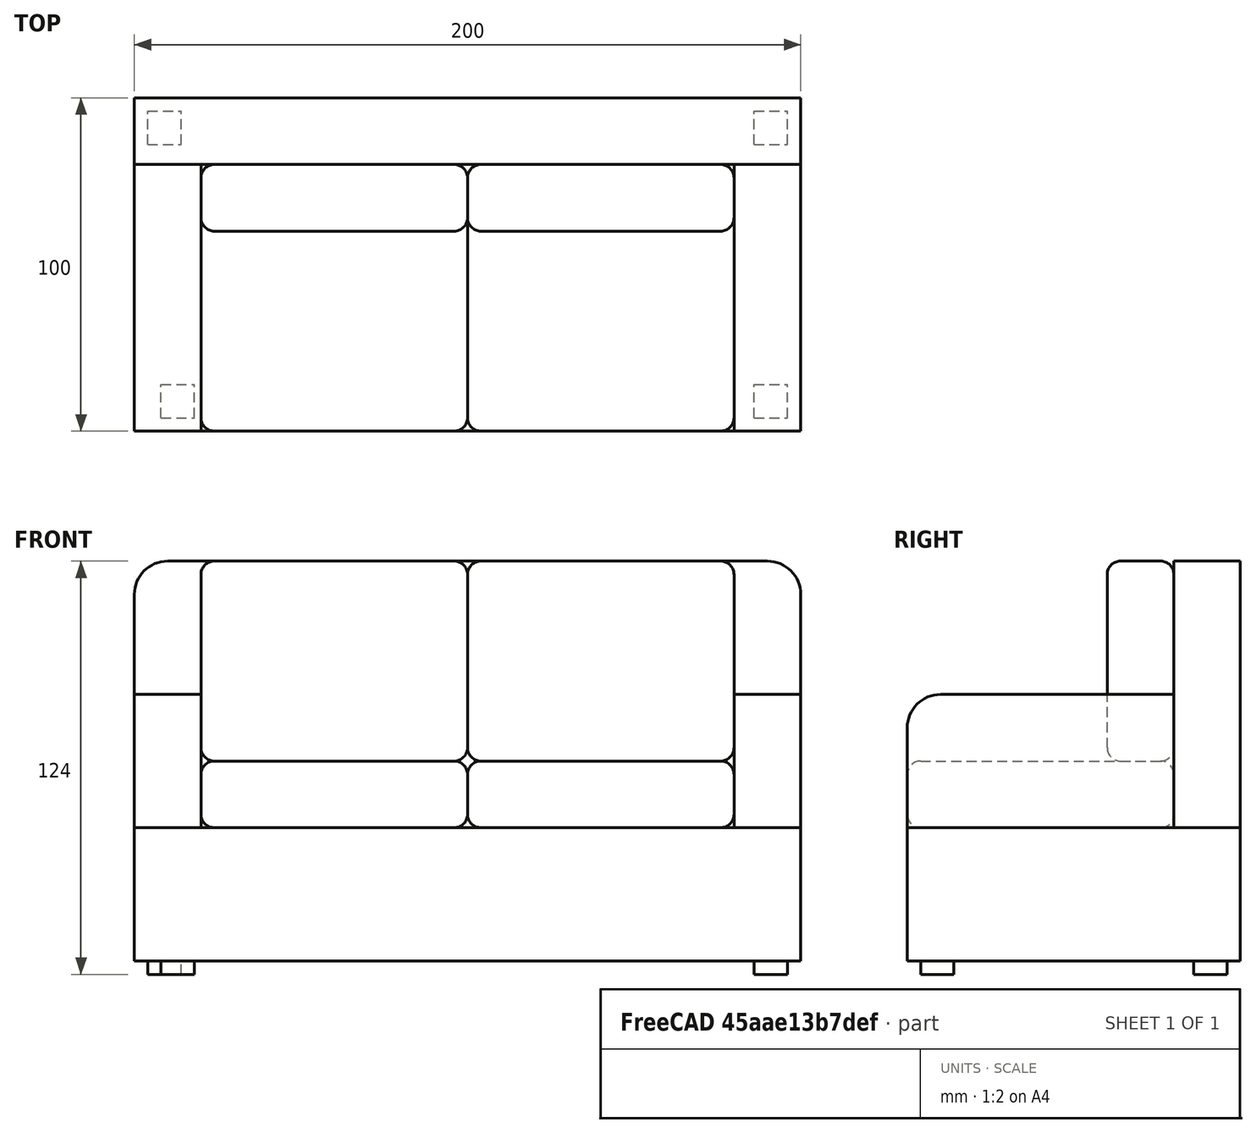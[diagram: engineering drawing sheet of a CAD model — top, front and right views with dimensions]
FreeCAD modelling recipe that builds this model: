
FCSTD DOCUMENT  (FreeCAD 0.21R33668 +26 (Git))
Label: canapé
License: All rights reserved
LicenseURL: http://en.wikipedia.org/wiki/All_rights_reserved
objects: Part::Box×12, Part::Fillet×7, Part::Compound×3
note: 22 computed .brp shape members not serialized (recipe doc carries the construction recipe); baked Part::Feature solids carry a one-line shape summary decoded from their .brp

FEATURE [Part::Box] Box  label="Cube"
  AttacherType = Attacher::AttachEngine3D
  Height = 40
  Length = 200
  Width = 100
FEATURE [Part::Box] Box001  label="Cube001"
  AttacherType = Attacher::AttachEngine3D
  Height = 40
  Length = 20
  Placement = pos=(0,0,40) rot=(0,0,1;0rad)
  Width = 80
FEATURE [Part::Fillet] Fillet
  Base = -> Box001
  Edges = 1 edges r=10: [Edge10]
FEATURE [Part::Box] Box002  label="Cube002"
  AttacherType = Attacher::AttachEngine3D
  Height = 40
  Length = 20
  Placement = pos=(0,0,40) rot=(0,0,1;0rad)
  Width = 80
FEATURE [Part::Fillet] Fillet001
  Base = -> Box002
  Edges = 1 edges r=10: [Edge10]
  Placement = pos=(180,0,0) rot=(0,0,1;0rad)
FEATURE [Part::Box] Box003  label="Cube003"
  AttacherType = Attacher::AttachEngine3D
  Height = 80
  Length = 200
  Placement = pos=(0,80,40) rot=(0,0,1;0rad)
  Width = 20
FEATURE [Part::Fillet] Fillet002
  Base = -> Box003
  Edges = 2 edges r=10: [Edge2,Edge6]
FEATURE [Part::Box] Box004  label="Cube004"
  AttacherType = Attacher::AttachEngine3D
  Height = 20
  Length = 80
  Placement = pos=(20,0,40) rot=(0,0,1;0rad)
  Width = 80
FEATURE [Part::Fillet] Fillet003
  Base = -> Box004
  Edges = 12 edges r=4: [Edge1,Edge2,Edge3,Edge4,Edge5,Edge6,Edge7,Edge8,Edge9,Edge10,Edge11,Edge12]
  Placement = pos=(80,0,0) rot=(0,0,1;0rad)
FEATURE [Part::Box] Box005  label="Cube005"
  AttacherType = Attacher::AttachEngine3D
  Height = 20
  Length = 80
  Placement = pos=(20,0,40) rot=(0,0,1;0rad)
  Width = 80
FEATURE [Part::Fillet] Fillet004
  Base = -> Box005
  Edges = 12 edges r=4: [Edge1,Edge2,Edge3,Edge4,Edge5,Edge6,Edge7,Edge8,Edge9,Edge10,Edge11,Edge12]
FEATURE [Part::Box] Box006  label="Cube006"
  AttacherType = Attacher::AttachEngine3D
  Height = 60
  Length = 80
  Placement = pos=(20,60,60) rot=(0,0,1;0rad)
  Width = 20
FEATURE [Part::Fillet] Fillet005
  Base = -> Box006
  Edges = 12 edges r=4: [Edge1,Edge2,Edge3,Edge4,Edge5,Edge6,Edge7,Edge8,Edge9,Edge10,Edge11,Edge12]
FEATURE [Part::Box] Box007  label="Cube007"
  AttacherType = Attacher::AttachEngine3D
  Height = 60
  Length = 80
  Placement = pos=(20,60,60) rot=(0,0,1;0rad)
  Width = 20
FEATURE [Part::Fillet] Fillet006
  Base = -> Box007
  Edges = 12 edges r=4: [Edge1,Edge2,Edge3,Edge4,Edge5,Edge6,Edge7,Edge8,Edge9,Edge10,Edge11,Edge12]
  Placement = pos=(80,0,0) rot=(0,0,1;0rad)
FEATURE [Part::Box] Box008  label="Cube008"
  AttacherType = Attacher::AttachEngine3D
  Height = 4
  Length = 10
  Placement = pos=(8,4,-4) rot=(0,0,1;0rad)
  Width = 10
FEATURE [Part::Box] Box009  label="Cube009"
  AttacherType = Attacher::AttachEngine3D
  Height = 4
  Length = 10
  Placement = pos=(4,86,-4) rot=(0,0,1;0rad)
  Width = 10
FEATURE [Part::Box] Box010  label="Cube010"
  AttacherType = Attacher::AttachEngine3D
  Height = 4
  Length = 10
  Placement = pos=(186,4,-4) rot=(0,0,1;0rad)
  Width = 10
FEATURE [Part::Box] Box011  label="Cube011"
  AttacherType = Attacher::AttachEngine3D
  Height = 4
  Length = 10
  Placement = pos=(186,86,-4) rot=(0,0,1;0rad)
  Width = 10
FEATURE [Part::Compound] Compound  label="Pieds"
  Links = -> [Box011,Box008,Box010,Box009]
FEATURE [Part::Compound] Compound001  label="Coussins"
  Links = -> [Fillet006,Fillet005,Fillet003,Fillet004]
FEATURE [Part::Compound] Compound002  label="Canape"
  Links = -> [Fillet001,Fillet002,Fillet,Box]
